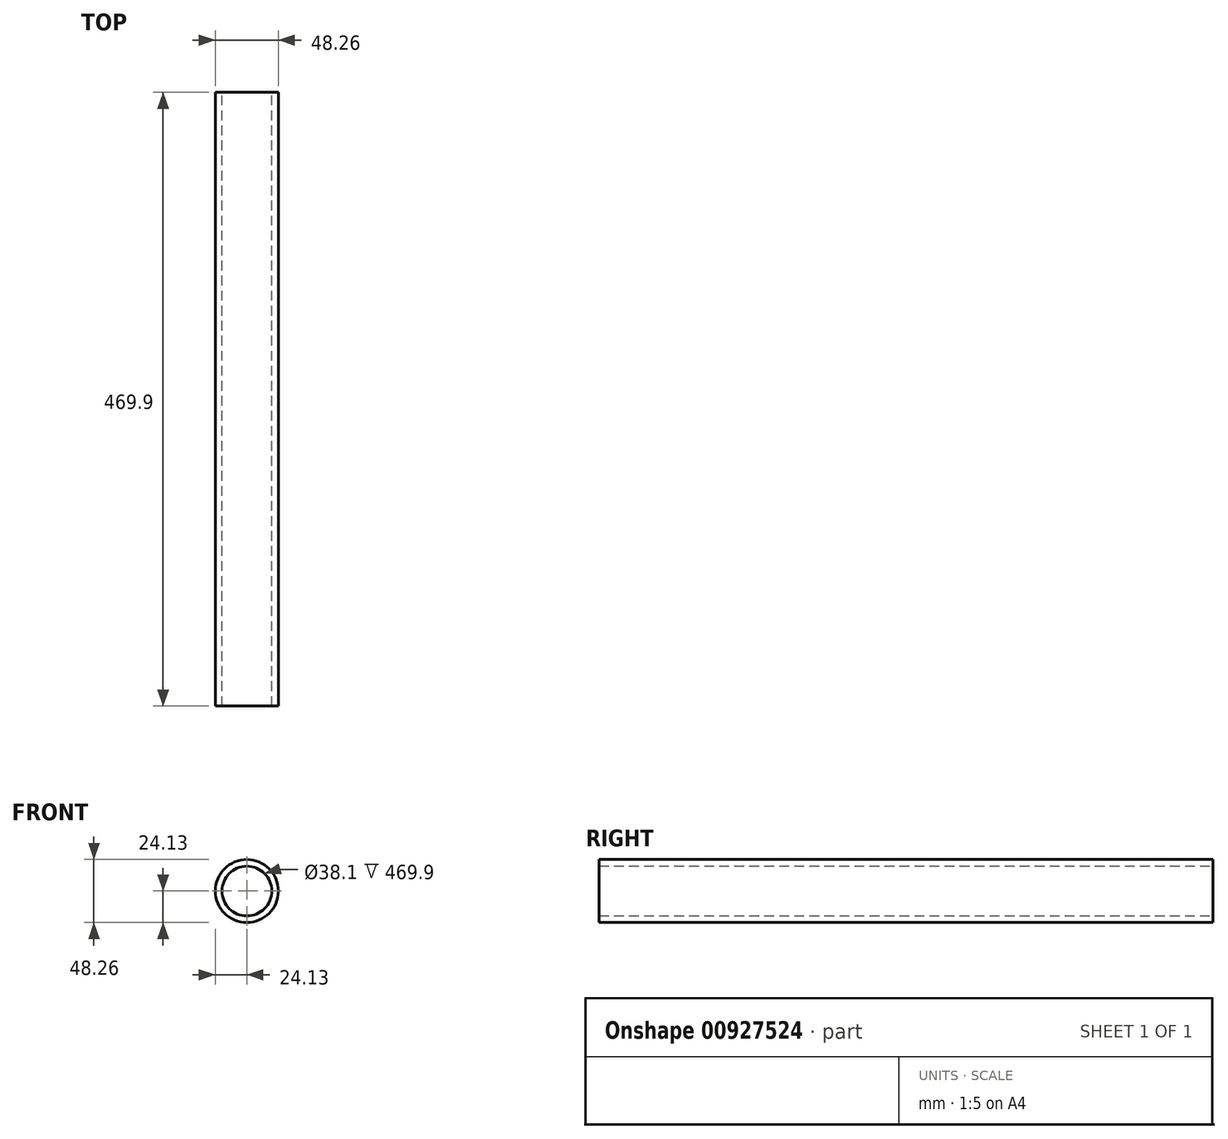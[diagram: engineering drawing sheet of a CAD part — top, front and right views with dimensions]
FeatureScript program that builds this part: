
annotation { "Feature Type Name" : "Feature", "Feature Type Description" : "" }
export const myFeature = defineFeature(function(context is Context, id is Id, definition is map)
    precondition{}
    {
        {
            var Q0;
            Q0=qCreatedBy(makeId("Front.planeOp"),FACE);
            var sketch = newSketch(context, id + "F0", { "sketchPlane" : qUnion([Q0])});
            skCircle(sketch, "E0", {"center": v(0, 0) * mm, "radius": 19.05 * mm});
            skCircle(sketch, "E1", {"center": v(0, 0) * mm, "radius": 24.13 * mm});
            skSolve(sketch);
        }
        {
            var Q0;
            Q0=qSketchRegion(id+"F0",true);
            var Q1;
            Q1=makeQuery(id+"F0.imprint","IMPRINT",FACE,{"disambiguationData":[TD([[makeQuery(id+"F0.imprint","IMPRINT",EDGE,{"derivedFrom":sQuery(id+"F0.wireOp",EDGE,"E0")}),-1.0]])]});
            extrude(context, id + "F1", {"entities" : qUnion([Q0, Q1]), "depth" : 469.9 * mm, "offsetDistance" : 25.4 * mm});
        }
    });
